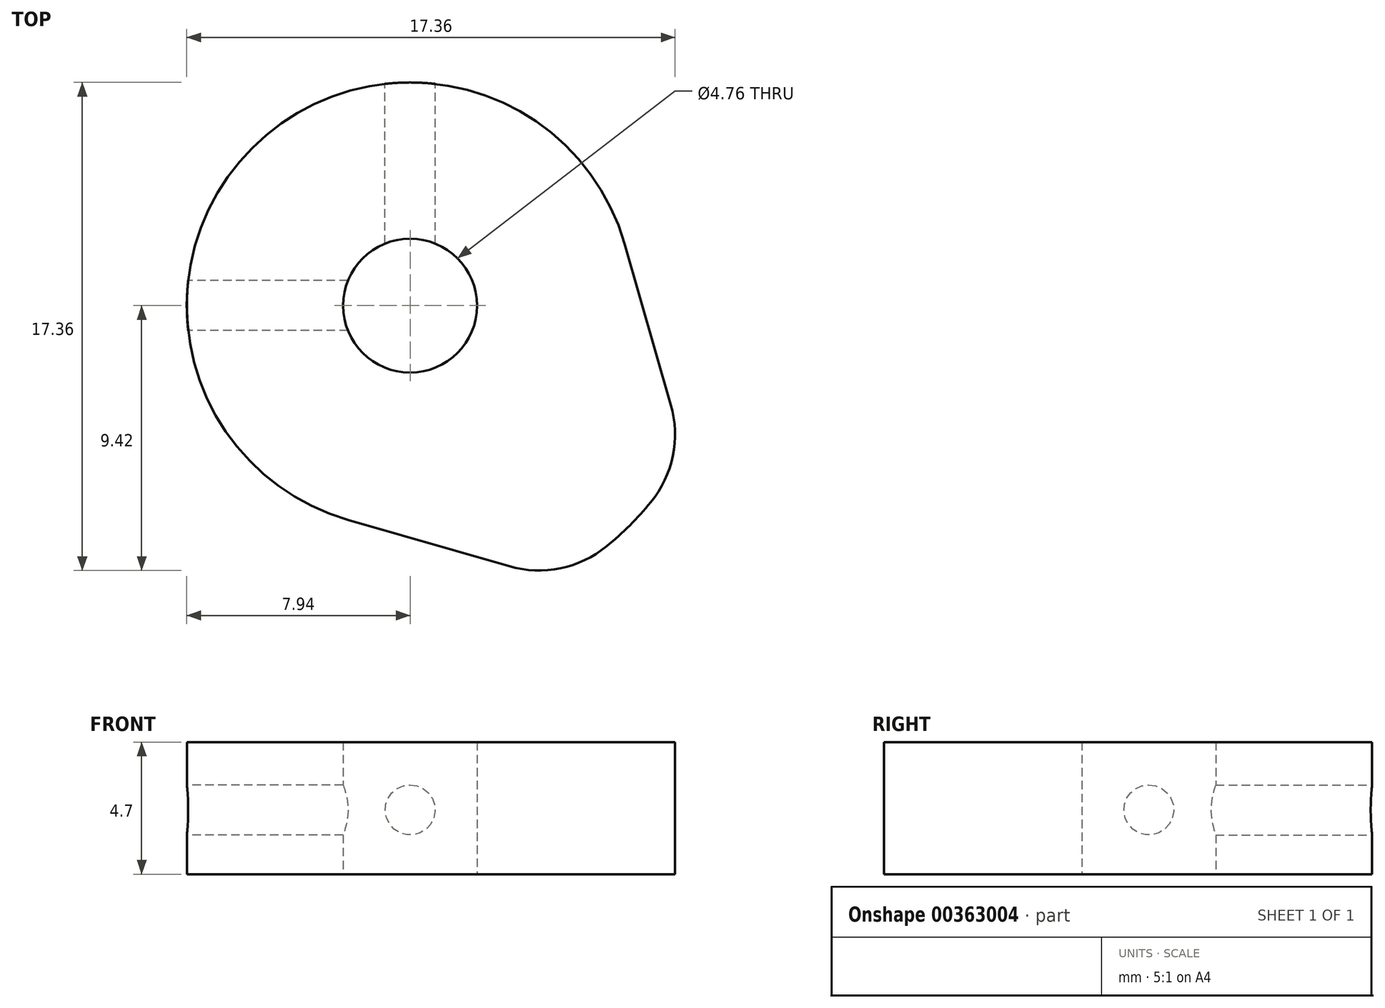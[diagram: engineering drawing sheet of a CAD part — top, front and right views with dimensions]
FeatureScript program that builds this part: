
annotation { "Feature Type Name" : "Feature", "Feature Type Description" : "" }
export const myFeature = defineFeature(function(context is Context, id is Id, definition is map)
    precondition{}
    {
        {
            var Q0;
            Q0=qCreatedBy(makeId("Top.planeOp"),FACE);
            var sketch = newSketch(context, id + "F0", { "sketchPlane" : qUnion([Q0])});
            skCircle(sketch, "E0", {"center": v(0, 0) * mm, "radius": 2.38 * mm});
            skArc(sketch, "E1", {"start": v(7.63, 2.19) * mm, "mid": v(-5.61, 5.61) * mm, "end": v(-2.19, -7.63) * mm});
            skArc(sketch, "E2", {"start": v(6.99, -8.56) * mm, "mid": v(7.81, -7.81) * mm, "end": v(8.56, -6.99) * mm});
            skLineSegment(sketch, "E3", {"start": v(-2.19, -7.63) * mm, "end": v(3.53, -9.27) * mm});
            skLineSegment(sketch, "E4", {"start": v(7.63, 2.19) * mm, "end": v(9.27, -3.53) * mm});
            skPoint(sketch, "E5.visualSharp", {"position": v(5.2, -9.75) * mm});
            skArc(sketch, "E5.filletArc", {"start": v(3.53, -9.27) * mm, "mid": v(5.35, -9.34) * mm, "end": v(6.99, -8.56) * mm});
            skPoint(sketch, "E6.visualSharp", {"position": v(9.75, -5.2) * mm});
            skArc(sketch, "E6.filletArc", {"start": v(8.56, -6.99) * mm, "mid": v(9.34, -5.35) * mm, "end": v(9.27, -3.53) * mm});
            skSolve(sketch);
        }
        {
            var Q0;
            Q0=makeQuery(id+"F0.imprint","IMPRINT",FACE,{"disambiguationData":[TD([[makeQuery(id+"F0.imprint","IMPRINT",EDGE,{"derivedFrom":sQuery(id+"F0.wireOp",EDGE,"E0")}),-1.0]])]});
            extrude(context, id + "F1", {"entities" : qUnion([Q0]), "depth" : 4.7 * mm});
        }
        {
            var Q0;
            Q0=qCreatedBy(makeId("Right.planeOp"),FACE);
            cPlane(context, id + "F2", {"entities" : qUnion([Q0]), "cplaneType" : CPlaneType.OFFSET, "offset" : 8.23 * mm, "oppositeDirection" : true, "width" : 152.4 * mm, "height" : 152.4 * mm});
        }
        {
            var Q0;
            Q0=qCreatedBy(id+"F2.planeOp",FACE);
            var sketch = newSketch(context, id + "F3", { "sketchPlane" : qUnion([Q0])});
            skPoint(sketch, "E7", {"position": v(0, 2.29) * mm});
            skSolve(sketch);
        }
        {
            var Q0;
            Q0=sQuery(id+"F3.wireOp",VERTEX,"E7");
            var Q1;
            Q1=makeQuery(id+"F1.opExtrude","SWEPT_BODY",BODY,{"disambiguationData":[OSD([sQuery(id+"F0.wireOp",EDGE,"E0"),sQuery(id+"F0.wireOp",EDGE,"E1"),sQuery(id+"F0.wireOp",EDGE,"E2"),sQuery(id+"F0.wireOp",EDGE,"E3"),sQuery(id+"F0.wireOp",EDGE,"E4"),sQuery(id+"F0.wireOp",EDGE,"E5.filletArc"),sQuery(id+"F0.wireOp",EDGE,"E6.filletArc")])]});
            hole(context, id + "F4", {"style" : HoleStyle.SIMPLE, "endStyle" : HoleEndStyle.BLIND, "oppositeDirection" : true, "standardTappedOrClearance" : lookupTablePath({ "standard" : "ANSI", "engagement" : "75%", "pitch" : "56 tpi", "size" : "#2", "type" : "Tapped" }), "standardBlindInLast" : lookupTablePath({ "standard" : "ANSI", "engagement" : "75%", "pitch" : "56 tpi", "size" : "#2", "type" : "Tapped" }), "holeDiameter" : 1.78 * mm, "showTappedDepth" : true, "holeDepth" : 8.48 * mm, "tappedDepth" : 7.12 * mm, "tapClearance" : 3, "locations" : qUnion([Q0]), "scope" : qUnion([Q1]), "majorDiameter" : 2.18 * mm});
        }
        {
            var Q0;
            Q0=qCreatedBy(makeId("Front.planeOp"),FACE);
            cPlane(context, id + "F5", {"entities" : qUnion([Q0]), "cplaneType" : CPlaneType.OFFSET, "offset" : 8.9 * mm, "oppositeDirection" : true, "width" : 152.4 * mm, "height" : 152.4 * mm});
        }
        {
            var Q0;
            Q0=qCreatedBy(id+"F5.planeOp",FACE);
            var sketch = newSketch(context, id + "F6", { "sketchPlane" : qUnion([Q0])});
            skPoint(sketch, "E8", {"position": v(0, 2.29) * mm});
            skSolve(sketch);
        }
        {
            var Q0;
            Q0=sQuery(id+"F6.wireOp",VERTEX,"E8");
            var Q1;
            Q1=makeQuery(id+"F1.opExtrude","SWEPT_BODY",BODY,{"disambiguationData":[OSD([sQuery(id+"F0.wireOp",EDGE,"E0"),sQuery(id+"F0.wireOp",EDGE,"E1"),sQuery(id+"F0.wireOp",EDGE,"E2"),sQuery(id+"F0.wireOp",EDGE,"E3"),sQuery(id+"F0.wireOp",EDGE,"E4"),sQuery(id+"F0.wireOp",EDGE,"E5.filletArc"),sQuery(id+"F0.wireOp",EDGE,"E6.filletArc")])]});
            hole(context, id + "F7", {"style" : HoleStyle.SIMPLE, "endStyle" : HoleEndStyle.BLIND, "oppositeDirection" : true, "standardTappedOrClearance" : lookupTablePath({ "standard" : "ANSI", "engagement" : "75%", "pitch" : "56 tpi", "size" : "#2", "type" : "Tapped" }), "standardBlindInLast" : lookupTablePath({ "standard" : "ANSI", "engagement" : "75%", "pitch" : "56 tpi", "size" : "#2", "type" : "Tapped" }), "holeDiameter" : 1.78 * mm, "showTappedDepth" : true, "holeDepth" : 8.48 * mm, "tappedDepth" : 7.12 * mm, "tapClearance" : 3, "locations" : qUnion([Q0]), "scope" : qUnion([Q1]), "majorDiameter" : 2.18 * mm});
        }
    });
